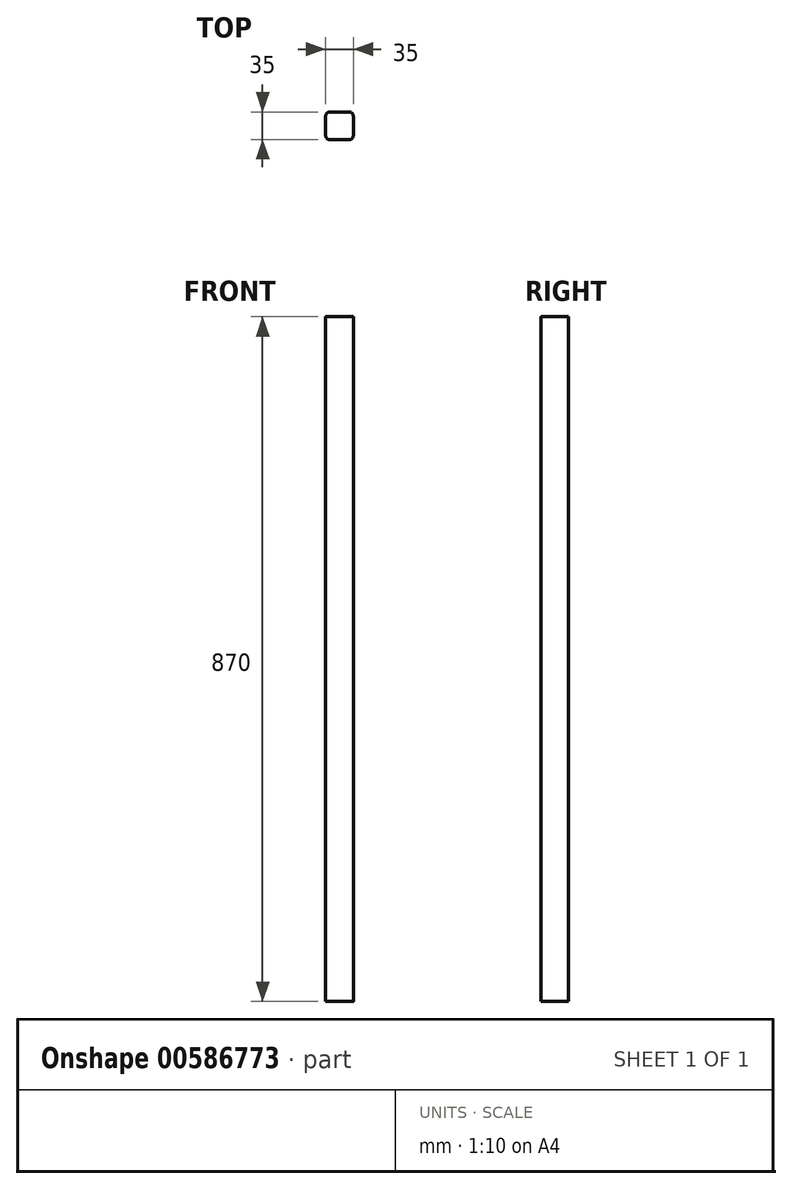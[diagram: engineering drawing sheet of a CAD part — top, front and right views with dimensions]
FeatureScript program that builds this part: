
annotation { "Feature Type Name" : "Feature", "Feature Type Description" : "" }
export const myFeature = defineFeature(function(context is Context, id is Id, definition is map)
    precondition{}
    {
        {
            var Q0;
            Q0=qCreatedBy(makeId("Top.planeOp"),FACE);
            var sketch = newSketch(context, id + "F0", { "sketchPlane" : qUnion([Q0])});
            skLineSegment(sketch, "E0.bottom", {"start": v(-12.5, 17.5) * mm, "end": v(12.5, 17.5) * mm});
            skLineSegment(sketch, "E0.top", {"start": v(-12.5, -17.5) * mm, "end": v(12.5, -17.5) * mm});
            skLineSegment(sketch, "E0.left", {"start": v(-17.5, 12.5) * mm, "end": v(-17.5, -12.5) * mm});
            skLineSegment(sketch, "E0.right", {"start": v(17.5, 12.5) * mm, "end": v(17.5, -12.5) * mm});
            skLineSegment(sketch, "E1", {"start": v(-17.5, 17.5) * mm, "end": v(17.5, -17.5) * mm, "construction": true});
            skPoint(sketch, "E2.visualSharp", {"position": v(-17.5, 17.5) * mm});
            skArc(sketch, "E2.filletArc", {"start": v(-12.5, 17.5) * mm, "mid": v(-16.04, 16.04) * mm, "end": v(-17.5, 12.5) * mm});
            skPoint(sketch, "E3.visualSharp", {"position": v(17.5, 17.5) * mm});
            skArc(sketch, "E3.filletArc", {"start": v(17.5, 12.5) * mm, "mid": v(16.04, 16.04) * mm, "end": v(12.5, 17.5) * mm});
            skPoint(sketch, "E4.visualSharp", {"position": v(17.5, -17.5) * mm});
            skArc(sketch, "E4.filletArc", {"start": v(12.5, -17.5) * mm, "mid": v(16.04, -16.04) * mm, "end": v(17.5, -12.5) * mm});
            skPoint(sketch, "E5.visualSharp", {"position": v(-17.5, -17.5) * mm});
            skArc(sketch, "E5.filletArc", {"start": v(-17.5, -12.5) * mm, "mid": v(-16.04, -16.04) * mm, "end": v(-12.5, -17.5) * mm});
            skSolve(sketch);
        }
        {
            var Q0;
            Q0 = qSketchRegion(id + "F0", true);
            extrude(context, id + "F1", {"entities" : qUnion([Q0]), "depth" : 870 * mm, "offsetDistance" : 25 * mm});
        }
    });
